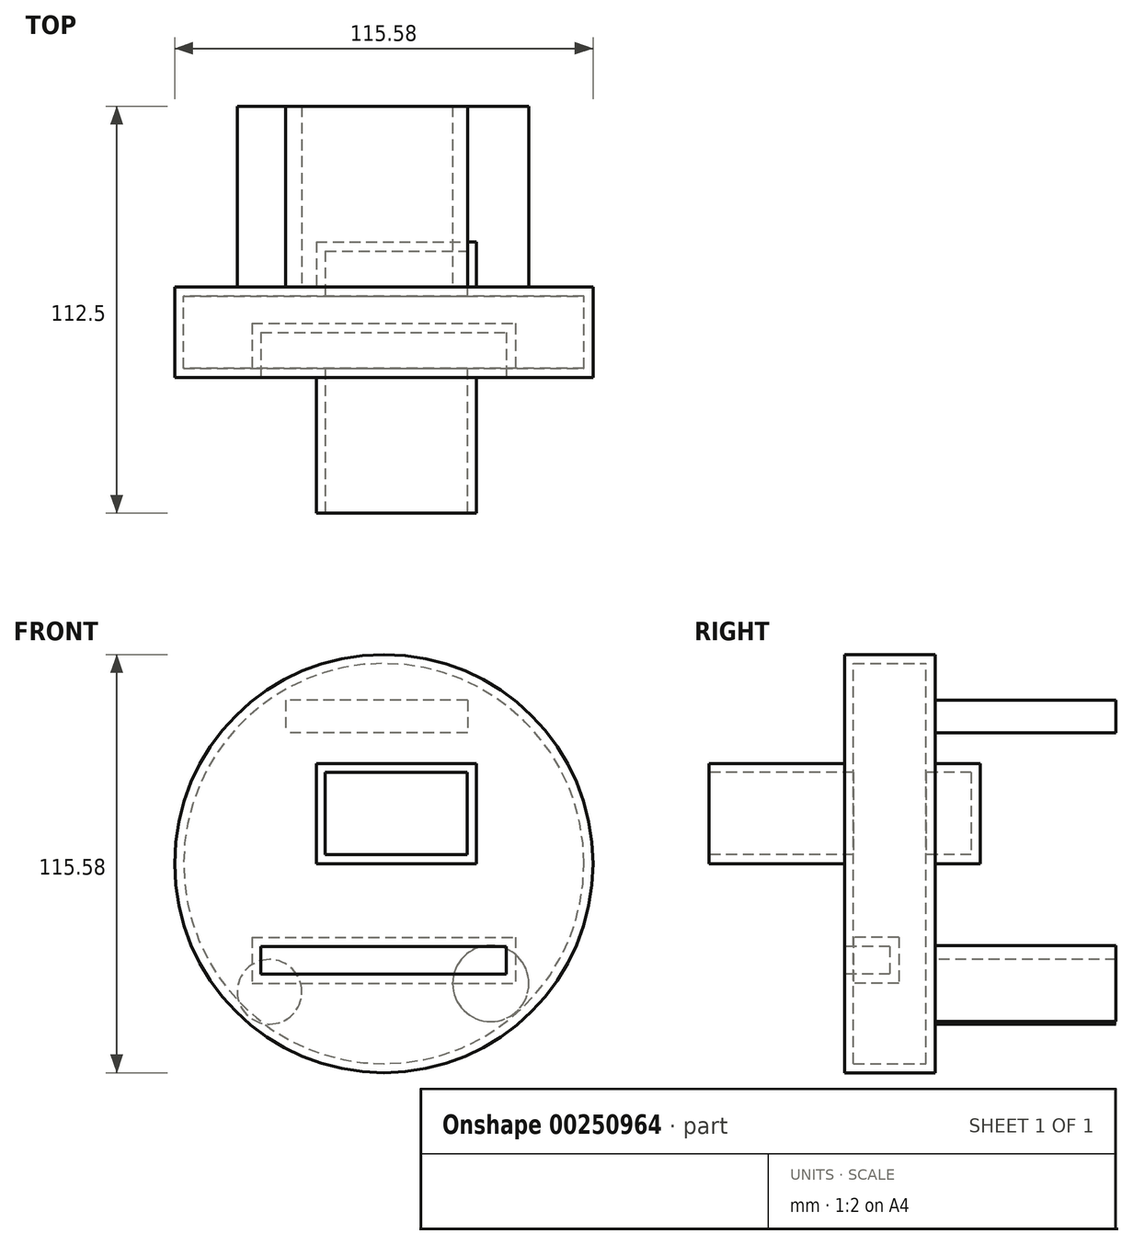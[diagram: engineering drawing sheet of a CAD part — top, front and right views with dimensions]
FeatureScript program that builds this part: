
annotation { "Feature Type Name" : "Feature", "Feature Type Description" : "" }
export const myFeature = defineFeature(function(context is Context, id is Id, definition is map)
    precondition{}
    {
        {
            var Q0;
            Q0=qCreatedBy(makeId("Front.planeOp"),FACE);
            var sketch = newSketch(context, id + "F0", { "sketchPlane" : qUnion([Q0])});
            skCircle(sketch, "E0", {"center": v(2.58, 0) * mm, "radius": 57.79 * mm});
            skSolve(sketch);
        }
        {
            var Q0;
            Q0=makeQuery(id+"F0.imprint","IMPRINT",FACE,{"disambiguationData":[TD([[makeQuery(id+"F0.imprint","IMPRINT",EDGE,{"derivedFrom":sQuery(id+"F0.wireOp",EDGE,"E0")}),1.0]])]});
            extrude(context, id + "F1", {"entities" : qUnion([Q0]), "endBound" : BoundingType.SYMMETRIC, "depth" : 25 * mm});
        }
        {
            var Q0;
            Q0=makeQuery(id+"F1.opExtrude","CAP_FACE",FACE,{"disambiguationData":[OSD([sQuery(id+"F0.wireOp",EDGE,"E0")])],"isStart":false});
            var sketch = newSketch(context, id + "F2", { "sketchPlane" : qUnion([Q0])});
            skLineSegment(sketch, "E1.bottom", {"start": v(-16.07, 27.68) * mm, "end": v(28.11, 27.68) * mm});
            skLineSegment(sketch, "E1.top", {"start": v(-16.07, 0) * mm, "end": v(28.11, 0) * mm});
            skLineSegment(sketch, "E1.left", {"start": v(-16.07, 27.68) * mm, "end": v(-16.07, 0) * mm});
            skLineSegment(sketch, "E1.right", {"start": v(28.11, 27.68) * mm, "end": v(28.11, 0) * mm});
            skSolve(sketch);
        }
        {
            var Q0;
            Q0=makeQuery(id+"F2.imprint","IMPRINT",FACE,{"disambiguationData":[TD([[makeQuery(id+"F2.imprint","IMPRINT",EDGE,{"derivedFrom":sQuery(id+"F2.wireOp",EDGE,"E1.bottom")}),1.0]])]});
            var sketch = newSketch(context, id + "F3", { "sketchPlane" : qUnion([Q0])});
            skLineSegment(sketch, "E2.bottom", {"start": v(-31.35, -22.86) * mm, "end": v(36.45, -22.86) * mm});
            skLineSegment(sketch, "E2.top", {"start": v(-31.35, -30.56) * mm, "end": v(36.45, -30.56) * mm});
            skLineSegment(sketch, "E2.left", {"start": v(-31.35, -22.86) * mm, "end": v(-31.35, -30.56) * mm});
            skLineSegment(sketch, "E2.right", {"start": v(36.45, -22.86) * mm, "end": v(36.45, -30.56) * mm});
            skSolve(sketch);
        }
        {
            var Q0;
            Q0=makeQuery(id+"F2.imprint","IMPRINT",FACE,{"disambiguationData":[TD([[makeQuery(id+"F2.imprint","IMPRINT",EDGE,{"derivedFrom":sQuery(id+"F2.wireOp",EDGE,"E1.bottom")}),-1.0]])]});
            extrude(context, id + "F4", {"entities" : qUnion([Q0]), "operationType" : NewBodyOperationType.ADD, "endBound" : BoundingType.SYMMETRIC, "oppositeDirection" : true, "depth" : 75 * mm});
        }
        {
            var Q0;
            Q0=makeQuery(id+"F3.imprint","IMPRINT",FACE,{"disambiguationData":[TD([[makeQuery(id+"F3.imprint","IMPRINT",EDGE,{"derivedFrom":sQuery(id+"F3.wireOp",EDGE,"E2.bottom")}),-1.0]])]});
            extrude(context, id + "F5", {"entities" : qUnion([Q0]), "operationType" : NewBodyOperationType.REMOVE, "endBound" : BoundingType.SYMMETRIC, "oppositeDirection" : true, "depth" : 25 * mm});
        }
        {
            var Q0;
            Q0=makeQuery(id+"F4.opExtrude","CAP_FACE",FACE,{"disambiguationData":[OSD([sQuery(id+"F2.wireOp",EDGE,"E1.bottom"),sQuery(id+"F2.wireOp",EDGE,"E1.top"),sQuery(id+"F2.wireOp",EDGE,"E1.left"),sQuery(id+"F2.wireOp",EDGE,"E1.right")])],"isStart":true});
            shell(context, id + "F6", {"entities" : qUnion([Q0]), "thickness" : 2.5 * mm});
        }
        {
            var Q0;
            Q0=makeQuery(id+"F1.opExtrude","CAP_FACE",FACE,{"disambiguationData":[OSD([sQuery(id+"F0.wireOp",EDGE,"E0")])],"isStart":true});
            var sketch = newSketch(context, id + "F7", { "sketchPlane" : qUnion([Q0])});
            skLineSegment(sketch, "E3.bottom", {"start": v(-25.69, 45.1) * mm, "end": v(24.56, 45.1) * mm});
            skLineSegment(sketch, "E3.top", {"start": v(-25.69, 36.17) * mm, "end": v(24.56, 36.17) * mm});
            skLineSegment(sketch, "E3.left", {"start": v(-25.69, 45.1) * mm, "end": v(-25.69, 36.17) * mm});
            skLineSegment(sketch, "E3.right", {"start": v(24.56, 45.1) * mm, "end": v(24.56, 36.17) * mm});
            skSolve(sketch);
        }
        {
            var Q0;
            Q0=makeQuery(id+"F7.imprint","IMPRINT",FACE,{"disambiguationData":[TD([[makeQuery(id+"F7.imprint","IMPRINT",EDGE,{"derivedFrom":sQuery(id+"F7.wireOp",EDGE,"E3.bottom")}),-1.0]])]});
            extrude(context, id + "F8", {"entities" : qUnion([Q0]), "operationType" : NewBodyOperationType.ADD, "depth" : 50 * mm});
        }
        {
            var Q0;
            Q0=makeQuery(id+"F1.opExtrude","CAP_FACE",FACE,{"disambiguationData":[OSD([sQuery(id+"F0.wireOp",EDGE,"E0")])],"isStart":true});
            var sketch = newSketch(context, id + "F9", { "sketchPlane" : qUnion([Q0])});
            skCircle(sketch, "E4", {"center": v(28.98, -35.43) * mm, "radius": 8.91 * mm});
            skSolve(sketch);
        }
        {
            var Q0;
            Q0=makeQuery(id+"F9.imprint","IMPRINT",FACE,{"disambiguationData":[TD([[makeQuery(id+"F9.imprint","IMPRINT",EDGE,{"derivedFrom":sQuery(id+"F9.wireOp",EDGE,"E4")}),-1.0]])]});
            var sketch = newSketch(context, id + "F10", { "sketchPlane" : qUnion([Q0])});
            skCircle(sketch, "E5", {"center": v(-32.13, -33.14) * mm, "radius": 10.53 * mm});
            skSolve(sketch);
        }
        {
            var Q0;
            Q0=makeQuery(id+"F10.imprint","IMPRINT",FACE,{"disambiguationData":[TD([[makeQuery(id+"F10.imprint","IMPRINT",EDGE,{"derivedFrom":sQuery(id+"F10.wireOp",EDGE,"E5")}),1.0]])]});
            extrude(context, id + "F11", {"entities" : qUnion([Q0]), "operationType" : NewBodyOperationType.ADD, "depth" : 50 * mm});
        }
        {
            var Q0;
            Q0=makeQuery(id+"F9.imprint","IMPRINT",FACE,{"disambiguationData":[TD([[makeQuery(id+"F9.imprint","IMPRINT",EDGE,{"derivedFrom":sQuery(id+"F9.wireOp",EDGE,"E4")}),1.0]])]});
            extrude(context, id + "F12", {"entities" : qUnion([Q0]), "operationType" : NewBodyOperationType.ADD, "depth" : 50 * mm});
        }
    });
